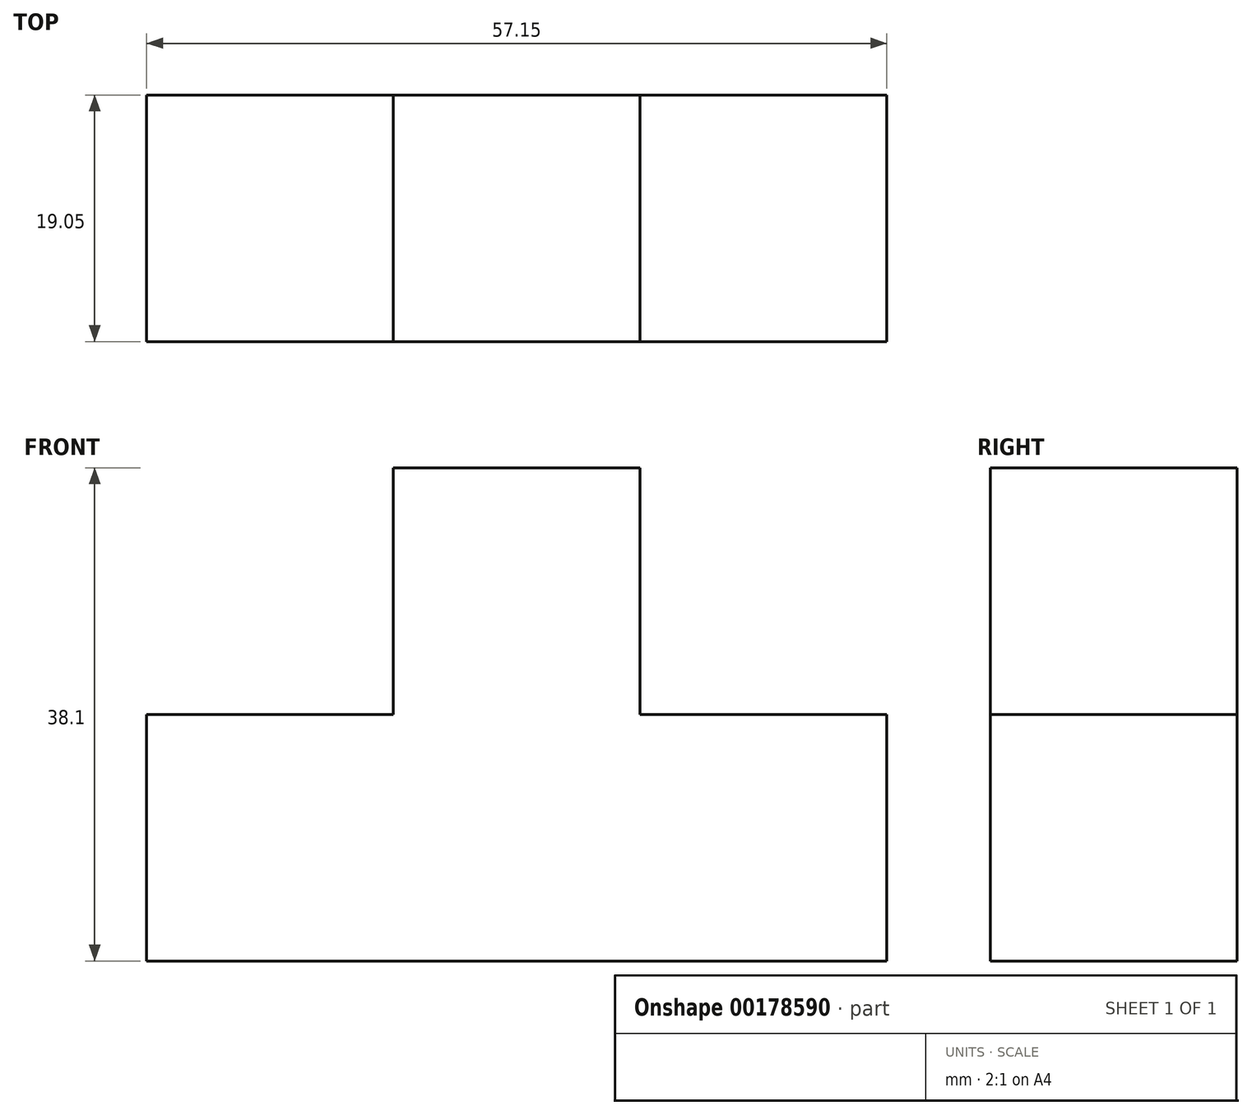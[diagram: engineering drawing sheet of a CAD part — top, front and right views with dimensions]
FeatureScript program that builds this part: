
annotation { "Feature Type Name" : "Feature", "Feature Type Description" : "" }
export const myFeature = defineFeature(function(context is Context, id is Id, definition is map)
    precondition{}
    {
        {
            var Q0;
            Q0=qCreatedBy(makeId("Front.planeOp"),FACE);
            var sketch = newSketch(context, id + "F0", { "sketchPlane" : qUnion([Q0])});
            skLineSegment(sketch, "E0", {"start": v(-38.1, 13.68) * mm, "end": v(-19.05, 13.68) * mm});
            skLineSegment(sketch, "E1", {"start": v(-19.05, 13.68) * mm, "end": v(-19.05, -5.37) * mm});
            skLineSegment(sketch, "E2", {"start": v(-19.05, -5.37) * mm, "end": v(-38.1, -5.37) * mm});
            skLineSegment(sketch, "E3", {"start": v(-38.1, -5.37) * mm, "end": v(-38.1, 13.68) * mm});
            skLineSegment(sketch, "E4", {"start": v(0, 13.68) * mm, "end": v(0, -5.37) * mm});
            skPoint(sketch, "E4.startSnap0", {"position": v(-28.57, 13.68) * mm});
            skLineSegment(sketch, "E5", {"start": v(0, -5.37) * mm, "end": v(-19.05, -5.37) * mm});
            skLineSegment(sketch, "E6", {"start": v(0, 13.68) * mm, "end": v(-19.05, 13.68) * mm});
            skLineSegment(sketch, "E7", {"start": v(19.05, 13.68) * mm, "end": v(19.05, -5.37) * mm});
            skLineSegment(sketch, "E8", {"start": v(19.05, -5.37) * mm, "end": v(0, -5.37) * mm});
            skLineSegment(sketch, "E9", {"start": v(0, 13.68) * mm, "end": v(19.05, 13.68) * mm});
            skLineSegment(sketch, "E10", {"start": v(-19.05, 13.68) * mm, "end": v(-19.05, 32.73) * mm});
            skLineSegment(sketch, "E11", {"start": v(-19.05, 32.73) * mm, "end": v(0, 32.73) * mm});
            skLineSegment(sketch, "E12", {"start": v(0, 32.73) * mm, "end": v(0, 13.68) * mm});
            skSolve(sketch);
        }
        {
            var Q0;
            Q0 = qSketchRegion(id + "F0", true);
            extrude(context, id + "F1", {"entities" : qUnion([Q0]), "depth" : 19.05 * mm});
        }
    });
